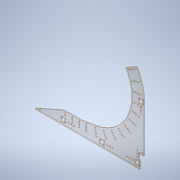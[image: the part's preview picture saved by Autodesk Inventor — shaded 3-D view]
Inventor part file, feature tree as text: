
AUTODESK INVENTOR PART (.ipt)
format: ipt  version: 2020 (Build 240168000, 168)  size: 521,216 bytes
history: native  units: in
note: dims shown in document units (in); Inventor stores cm internally (conversion verified against a paired STEP export)
features: extrude x5, sketch x4, fillet x1
ambient origin geometry x8: Origin, YZ Plane, XZ Plane, XY Plane, X Axis, Y Axis, Z Axis, Center Point
bodies: Solid1 (feature_tree)
feature tree (10):
  extrude  "Extrusion1"  Depth=0.25in
  extrude  "Extrusion2"  Depth=0.25in TaperAngle=0.0deg
  extrude  "Extrusion3"  TaperAngle=0.0deg  [1 undecoded]
  fillet  "Fillet1"  Radius=0.125in
  extrude  "Extrusion4"  Depth=0.5in
  extrude  "Extrusion5"  Depth=2.0in
  sketch  "Sketch1"  dims[d0=0.25in d1=0.0in d2=0.25in]
  sketch  "Sketch2"  dims[d3=0.5in d4=0.25in d5=0.0in]
  sketch  "Sketch3"  dims[d6=0.3in d7=0.0in d8=0.0in d9=0.125in]
  sketch  "Sketch4"  dims[d10=0.2031in d11=0.5in d12=2.0in d13=0.5in d14=0.5in d15=0.5in d16=0.5in d17=13.134in d18=0.5in d19=0.5in d20=4.7244in d22=120.0deg d24=1.5748in d26=2.0in d27=0.3937in d29=1.0in d31=1.0in d32=0.0in d33=0.25in d34=1.0in d35=0.0in]
note: 1 required parameter value undecoded (feature->parameter linkage not recoverable at this tier; creation-order binding heuristic only, values carry confidence <= 0.55)
